FCSTD DOCUMENT  (FreeCAD 0.21R33694 (Git))
Label: land-marking-calculation (copy)
License: All rights reserved
LicenseURL: http://en.wikipedia.org/wiki/All_rights_reserved
objects: Sketcher::SketchObject×4, PartDesign::Body×3
note: 7 computed .brp shape members not serialized (recipe doc carries the construction recipe); baked Part::Feature solids carry a one-line shape summary decoded from their .brp

FEATURE [Sketcher::SketchObject] Sketch
  FullyConstrained = true
  MapMode = 5
  Support = -> [XY_Plane]
  sketch-geometry (10):
    g0: LineSegment StartX=3.89e-14 StartY=-1e-16 StartZ=0 EndX=865.999 EndY=-1.39277 EndZ=0
    g1: LineSegment StartX=865.999 StartY=-1.39277 StartZ=0 EndX=893.591 EndY=426.719 EndZ=0
    g2: LineSegment StartX=893.591 StartY=426.719 StartZ=0 EndX=30.6757 EndY=470 EndZ=0
    g3: LineSegment StartX=30.6757 StartY=470 StartZ=0 EndX=4.26e-14 EndY=0 EndZ=0
    g4: LineSegment StartX=30.6757 StartY=470 StartZ=0 EndX=30.6757 EndY=0 EndZ=0
    g5: LineSegment StartX=668.676 StartY=438 StartZ=0 EndX=668.676 EndY=0 EndZ=0
    g6: GeomPoint X=865.999 Y=2.3e-15 Z=0
    g7: GeomPoint X=30.6757 Y=-0.0493353 Z=0
    g8: GeomPoint X=30.6757 Y=438 Z=0
    g9: LineSegment StartX=30.6757 StartY=438 StartZ=0 EndX=668.676 EndY=438 EndZ=0
  constraints (33):
    c: Coincident(g-1,g0)
    c: Coincident(g0,g1)
    c: Coincident(g1,g2)
    c: Coincident(g2,g3)
    c: Coincident(g3,g0)
    c: Distance(g3) = 471
    c: Distance(g1) = 429
    c: Distance(g2) = 864
    c: Coincident(g4,g2)
    c: DistanceX(g4,g5) = 638
    c: PointOnObject(g5,g2)
    c: Distance(g0,g0) = 866
    c: DistanceY(g4,g4) = 470
    c: Parallel(g5,g4)
    c: PointOnObject(g4,g-1)
    c: PointOnObject(g5,g-1)
    c: Perpendicular(g4,g-1)
    c: Angle(g4,g-1) = 1.5708
    c: DistanceY(g5,g5) = 438
    c: PointOnObject(g6,g-1)
    c: Vertical(g0,g6)
    c: Distance(g6,g0) = 1.39277
    c: DistanceX(g0,g4) = 30.6757
    c: PointOnObject(g7,g0)
    c: Vertical(g7,g4)
    c: PointOnObject(g8,g4)
    c: Horizontal(g8,g5)
    c: DistanceY(g8,g2) = 32
    c: Coincident(g9,g8)
    c: Coincident(g9,g5)
    c: Distance(g2,g5) = 638.802
    c: Distance(g5,g1) = 225.198
    c: Distance(g5,g0) = 197.328
FEATURE [PartDesign::Body] Body
  Group = -> [Sketch]
  Origin = -> Origin
FEATURE [Sketcher::SketchObject] Sketch001  label="y-axis-marks"
  FullyConstrained = false
  MapMode = 5
  Support = -> [XY_Plane001]
  sketch-geometry (13):
    g0: LineSegment StartX=1219.2 StartY=1219.2 StartZ=0 EndX=2053.72 EndY=13153.5 EndZ=0
    g1: LineSegment StartX=2053.72 StartY=13153.5 StartZ=0 EndX=23969.2 EndY=12004.9 EndZ=0
    g2: LineSegment StartX=23969.2 StartY=12004.9 StartZ=0 EndX=23215 EndY=1219.2 EndZ=0
    g3: LineSegment StartX=23215 StartY=1219.2 StartZ=0 EndX=1219.2 EndY=1219.2 EndZ=0
    g4: LineSegment StartX=23215 StartY=1219.2 StartZ=0 EndX=23129.8 EndY=0 EndZ=0
    g5: LineSegment StartX=2053.72 StartY=13153.5 StartZ=0 EndX=0 EndY=13261.1 EndZ=0
    g6: LineSegment StartX=0 StartY=1327.15 StartZ=0 EndX=27519.6 EndY=1327.15 EndZ=0
    g7: LineSegment StartX=0 StartY=3079.75 StartZ=0 EndX=28776.8 EndY=3079.75 EndZ=0
    g8: LineSegment StartX=0 StartY=6051.55 StartZ=0 EndX=30453.1 EndY=6051.55 EndZ=0
    g9: LineSegment StartX=0 StartY=7804.15 StartZ=0 EndX=31740.3 EndY=7804.15 EndZ=0
    g10: LineSegment StartX=0 StartY=8032.75 StartZ=0 EndX=33087.3 EndY=8032.75 EndZ=0
    g11: LineSegment StartX=0 StartY=9302.75 StartZ=0 EndX=35494.4 EndY=9302.75 EndZ=0
    g12: LineSegment StartX=0 StartY=11264.9 StartZ=0 EndX=38714.9 EndY=11264.9 EndZ=0
  constraints (44):
    c: Coincident(g0,g1)
    c: Coincident(g1,g2)
    c: Coincident(g2,g3)
    c: Horizontal(g3)
    c: Coincident(g0,g3)
    c: Angle(g3,g0) = 1.50098
    c: Angle(g0,g1) = 1.58825
    c: Angle(g1,g2) = 1.55334
    c: Angle(g2,g3) = 1.64061
    c: Distance(g1) = 21945.6
    c: Distance(g0) = 11963.4
    c: Distance(g2) = 10812.1
    c: Distance(g3) = 21995.8
    c: Coincident(g4,g2)
    c: PointOnObject(g4,g-1)
    c: Coincident(g5,g0)
    c: PointOnObject(g5,g-2)
    c: Parallel(g5,g1)
    c: Parallel(g2,g4)
    c: Distance(g5,g0) = 2056.54
    c: Distance(g2,g4) = 1222.18
    c: DistanceX(g-1,g0) = 1219.2
    c: DistanceY(g-1,g0) = 1219.2
    c: PointOnObject(g6,g-2)
    c: Horizontal(g6)
    c: DistanceY(g-1,g6) = 1327.15  'L14'
    c: PointOnObject(g7,g-2)
    c: Horizontal(g7)
    c: DistanceY(g6,g7) = 1752.6
    c: PointOnObject(g8,g-2)
    c: Horizontal(g8)
    c: DistanceY(g7,g8) = 2971.8  'L11'
    c: PointOnObject(g9,g-2)
    c: Horizontal(g9)
    c: DistanceY(g8,g9) = 1752.6  'L10'
    c: PointOnObject(g10,g-2)
    c: Horizontal(g10)
    c: DistanceY(g9,g10) = 228.6  'L9'
    c: PointOnObject(g11,g-2)
    c: Horizontal(g11)
    c: DistanceY(g10,g11) = 1270  'L8'
    c: PointOnObject(g12,g-2)
    c: Horizontal(g12)
    c: DistanceY(g11,g12) = 1962.15
FEATURE [Sketcher::SketchObject] Sketch002  label="matrix"
  FullyConstrained = false
  MapMode = 5
  Support = -> [XY_Plane001]
  sketch-geometry (41):
    g0: LineSegment StartX=1219.2 StartY=1219.2 StartZ=0 EndX=2007.72 EndY=13156.6 EndZ=0
    g1: LineSegment StartX=2007.72 StartY=13156.6 StartZ=0 EndX=23927.5 EndY=12092.5 EndZ=0
    g2: LineSegment StartX=23927.5 StartY=12092.5 StartZ=0 EndX=23215.6 EndY=1219.2 EndZ=0
    g3: LineSegment StartX=23215.6 StartY=1219.2 StartZ=0 EndX=1219.2 EndY=1219.2 EndZ=0
    g4: LineSegment StartX=23215.6 StartY=1219.2 StartZ=0 EndX=23135.8 EndY=4.0927e-12 EndZ=0
    g5: LineSegment StartX=2007.72 StartY=13156.6 StartZ=0 EndX=-9.095e-13 EndY=13254 EndZ=0
    g6: LineSegment StartX=1327.15 StartY=0 StartZ=0 EndX=1327.15 EndY=13189.6 EndZ=0
    g7: LineSegment StartX=1447.8 StartY=0 StartZ=0 EndX=1447.8 EndY=13183.8 EndZ=0
    g8: LineSegment StartX=1752.6 StartY=0 StartZ=0 EndX=1752.6 EndY=13169 EndZ=0
    g9: LineSegment StartX=1981.2 StartY=0 StartZ=0 EndX=1981.2 EndY=13157.9 EndZ=0
    g10: LineSegment StartX=4102.1 StartY=0 StartZ=0 EndX=4102.1 EndY=13054.9 EndZ=0
    g11: LineSegment StartX=2095.5 StartY=0 StartZ=0 EndX=2095.5 EndY=13152.3 EndZ=0
    g12: LineSegment StartX=6667.5 StartY=0 StartZ=0 EndX=6667.5 EndY=10301.8 EndZ=0
    g13: LineSegment StartX=0 StartY=1333.5 StartZ=0 EndX=8152.68 EndY=1333.5 EndZ=0
    g14: LineSegment StartX=0 StartY=3086.1 StartZ=0 EndX=23337.8 EndY=3086.1 EndZ=0
    g15: LineSegment StartX=0 StartY=6057.9 StartZ=0 EndX=23532.4 EndY=6057.9 EndZ=0
    g16: LineSegment StartX=0 StartY=8039.1 StartZ=0 EndX=23662.1 EndY=8039.1 EndZ=0
    g17: LineSegment StartX=0 StartY=7810.5 StartZ=0 EndX=23647.2 EndY=7810.5 EndZ=0
    g18: LineSegment StartX=0 StartY=9309.1 StartZ=0 EndX=23745.3 EndY=9309.1 EndZ=0
    g19: LineSegment StartX=0 StartY=11271.2 StartZ=0 EndX=23873.7 EndY=11271.2 EndZ=0
    g20: GeomPoint X=1327.15 Y=1333.5 Z=0
    g21: GeomPoint X=1447.8 Y=3086.1 Z=0
    g22: GeomPoint X=1752.6 Y=6057.9 Z=0
    g23: GeomPoint X=1981.2 Y=9309.1 Z=0
    g24: GeomPoint X=2095.5 Y=11271.2 Z=0
    g25: GeomPoint X=1883.18 Y=11271.2 Z=0
    g26: GeomPoint X=1753.58 Y=9309.1 Z=0
    g27: GeomPoint X=1538.82 Y=6057.9 Z=0
    g28: GeomPoint X=1342.52 Y=3086.1 Z=0
    g29: GeomPoint X=1226.75 Y=1333.5 Z=0
    g30: LineSegment StartX=8140.7 StartY=0 StartZ=0 EndX=8140.7 EndY=12858.9 EndZ=0
    g31: LineSegment StartX=8369.3 StartY=0 StartZ=0 EndX=8369.3 EndY=11675.8 EndZ=0
    g32: LineSegment StartX=10350.5 StartY=0 StartZ=0 EndX=10350.5 EndY=11614.6 EndZ=0
    g33: LineSegment StartX=11684 StartY=0 StartZ=0 EndX=11684 EndY=11798.3 EndZ=0
    g34: LineSegment StartX=11912.6 StartY=0 StartZ=0 EndX=11912.6 EndY=12675.8 EndZ=0
    g35: LineSegment StartX=13563.6 StartY=0 StartZ=0 EndX=13563.6 EndY=12595.6 EndZ=0
    g36: LineSegment StartX=18034 StartY=0 StartZ=0 EndX=18034 EndY=12378.6 EndZ=0
    g37: GeomPoint X=2007.44 Y=13152.3 Z=0
    g38: LineSegment StartX=0 StartY=12922.2 StartZ=0 EndX=2095.5 EndY=12922.2 EndZ=0
    g39: GeomPoint X=1992.24 Y=12922.2 Z=0
    g40: GeomPoint X=18034 Y=1219.2 Z=0
  constraints (149):
    c: Coincident(g0,g1)
    c: Coincident(g1,g2)
    c: Coincident(g2,g3)
    c: Horizontal(g3)
    c: Coincident(g0,g3)
    c: Angle(g0,g1) = 1.58825
    c: Distance(g1) = 21945.6
    c: Distance(g0) = 11963.4
    c: Distance(g2) = 10896.6
    c: Distance(g3) = 21996.4
    c: Coincident(g4,g2)
    c: PointOnObject(g4,g-1)
    c: Coincident(g5,g0)
    c: PointOnObject(g5,g-2)
    c: Parallel(g5,g1)
    c: Parallel(g2,g4)
    c: Distance(g5,g0) = 2010.08
    c: Distance(g2,g4) = 1221.81
    c: DistanceX(g-1,g0) = 1219.2
    c: DistanceY(g-1,g0) = 1219.2
    c: PointOnObject(g6,g-1)
    c: Vertical(g6)
    c: DistanceX(g-1,g6) = 1327.15
    c: PointOnObject(g7,g-1)
    c: Vertical(g7)
    c: DistanceX(g6,g7) = 120.65
    c: PointOnObject(g8,g-1)
    c: Vertical(g8)
    c: DistanceX(g7,g8) = 304.8
    c: PointOnObject(g9,g-1)
    c: Vertical(g9)
    c: DistanceX(g8,g9) = 228.6
    c: PointOnObject(g10,g-1)
    c: Vertical(g10)
    c: PointOnObject(g11,g-1)
    c: Vertical(g11)
    c: DistanceX(g9,g11) = 114.3
    c: DistanceX(g11,g10) = 2006.6
    c: PointOnObject(g12,g-1)
    c: Vertical(g12)
    c: DistanceX(g10,g12) = 2565.4
    c: PointOnObject(g13,g-2)
    c: Horizontal(g13)
    c: PointOnObject(g14,g-2)
    c: Horizontal(g14)
    c: PointOnObject(g15,g-2)
    c: Horizontal(g15)
    c: PointOnObject(g16,g-2)
    c: Horizontal(g16)
    c: PointOnObject(g17,g-2)
    c: Horizontal(g17)
    c: DistanceY(g-1,g13) = 1333.5
    c: DistanceY(g13,g14) = 1752.6
    c: DistanceY(g14,g15) = 2971.8
    c: DistanceY(g15,g17) = 1752.6
    c: DistanceY(g17,g16) = 228.6
    c: PointOnObject(g18,g-2)
    c: Horizontal(g18)
    c: PointOnObject(g19,g-2)
    c: Horizontal(g19)
    c: DistanceY(g16,g18) = 1270
    c: DistanceY(g18,g19) = 1962.15
    c: PointOnObject(g20,g13)
    c: PointOnObject(g20,g6)
    c: PointOnObject(g21,g14)
    c: PointOnObject(g21,g7)
    c: PointOnObject(g22,g8)
    c: PointOnObject(g22,g15)
    c: PointOnObject(g23,g18)
    c: PointOnObject(g23,g9)
    c: PointOnObject(g24,g11)
    c: PointOnObject(g24,g19)
    c: PointOnObject(g25,g0)
    c: Horizontal(g24,g25)
    c: PointOnObject(g26,g0)
    c: Horizontal(g23,g26)
    c: PointOnObject(g27,g0)
    c: Horizontal(g22,g27)
    c: PointOnObject(g28,g0)
    c: Horizontal(g21,g28)
    c: PointOnObject(g29,g0)
    c: Horizontal(g20,g29)
    c: PointOnObject(g6,g5)
    c: PointOnObject(g7,g5)
    c: PointOnObject(g8,g5)
    c: PointOnObject(g9,g5)
    c: PointOnObject(g11,g1)
    c: Distance(g7,g8) = 305.159
    c: Distance(g6,g7) = 120.792
    c: Distance(g8,g9) = 228.869
    c: Distance(g9,g11) = 114.435
    c: Distance(g6,g5) = 1328.71
    c: PointOnObject(g10,g1)
    c: Distance(g11,g10) = 2008.96
    c: PointOnObject(g30,g-1)
    c: Vertical(g30)
    c: DistanceX(g12,g30) = 1473.2
    c: PointOnObject(g30,g1)
    c: PointOnObject(g31,g-1)
    c: Vertical(g31)
    c: DistanceX(g30,g31) = 228.6
    c: PointOnObject(g32,g-1)
    c: Vertical(g32)
    c: DistanceX(g31,g32) = 1981.2
    c: PointOnObject(g33,g-1)
    c: Vertical(g33)
    c: DistanceX(g32,g33) = 1333.5
    c: PointOnObject(g34,g-1)
    c: Vertical(g34)
    c: DistanceX(g33,g34) = 228.6
    c: PointOnObject(g35,g-1)
    c: Vertical(g35)
    c: DistanceX(g34,g35) = 1651
    c: PointOnObject(g36,g-1)
    c: Vertical(g36)
    c: DistanceX(g35,g36) = 4470.4
    c: PointOnObject(g34,g1)
    c: PointOnObject(g35,g1)
    c: PointOnObject(g36,g1)
    c: Distance(g35,g36) = 4475.66
    c: Distance(g10,g30) = 4043.36
    c: Distance(g30,g34) = 3776.34
    c: Distance(g34,g35) = 1652.94
    c: PointOnObject(g19,g2)
    c: PointOnObject(g18,g2)
    c: PointOnObject(g16,g2)
    c: PointOnObject(g17,g2)
    c: PointOnObject(g15,g2)
    c: PointOnObject(g14,g2)
    c: Distance(g27,g28) = 2978.28
    c: Distance(g29,g0) = 114.549
    c: Distance(g29,g28) = 1756.42
    c: Distance(g26,g27) = 3258.29
    c: Distance(g25,g26) = 1966.43
    c: PointOnObject(g37,g0)
    c: Horizontal(g11,g37)
    c: PointOnObject(g38,g-2)
    c: Horizontal(g38)
    c: DistanceY(g19,g38) = 1651
    c: PointOnObject(g38,g11)
    c: PointOnObject(g39,g0)
    c: Horizontal(g38,g39)
    c: Distance(g39,g25) = 1654.6
    c: Distance(g29,g-1) = 1811.94
    c: Distance(g5,g-1) = 13254
    c: DistanceX(g-1,g4) = 23135.8
    c: PointOnObject(g40,g36)
    c: PointOnObject(g40,g3)
    c: DistanceY(g40,g36) = 11159.4
FEATURE [PartDesign::Body] Body001  label="center-line-align"
  Group = -> [Sketch001,Sketch002]
  Origin = -> Origin001
FEATURE [Sketcher::SketchObject] Sketch003
  FullyConstrained = false
  MapMode = 5
  Support = -> [XY_Plane002]
  sketch-geometry (2):
    g0: ArcOfCircle CenterX=0 CenterY=13583.8 CenterZ=0 NormalX=0 NormalY=0 NormalZ=1 AngleXU=0 Radius=11963.4 StartAngle=4.07637 EndAngle=4.54351
    g1: ArcOfCircle CenterX=17619.6 CenterY=1783.34 CenterZ=0 NormalX=0 NormalY=0 NormalZ=1 AngleXU=0 Radius=21996.4 StartAngle=2.97176 EndAngle=3.28114
  constraints (4):
    c: Radius(g0) = 11963.4
    c: Radius(g1) = 21996.4
    c: PointOnObject(g0,g-2)
    c: DistanceY(g0) = 13583.8
FEATURE [PartDesign::Body] Body002
  Group = -> [Sketch003]
  Origin = -> Origin002
